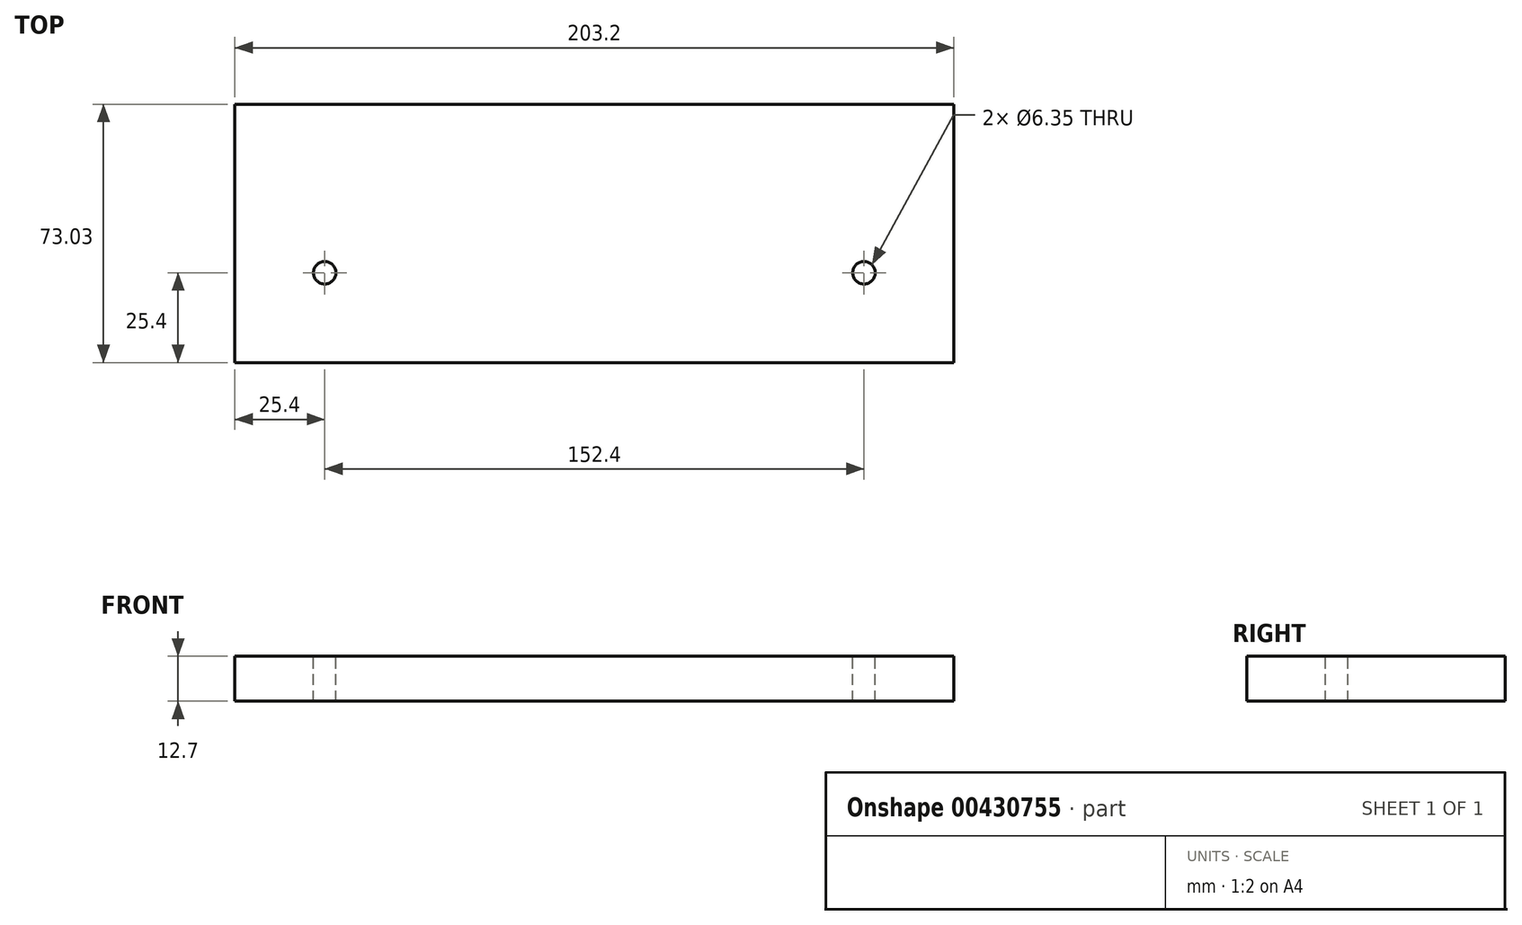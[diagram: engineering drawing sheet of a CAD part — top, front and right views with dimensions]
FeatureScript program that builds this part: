
annotation { "Feature Type Name" : "Feature", "Feature Type Description" : "" }
export const myFeature = defineFeature(function(context is Context, id is Id, definition is map)
    precondition{}
    {
        {
            var Q0;
            Q0=qCreatedBy(makeId("Top.planeOp"),FACE);
            var sketch = newSketch(context, id + "F0", { "sketchPlane" : qUnion([Q0])});
            skLineSegment(sketch, "E0.bottom", {"start": v(0, 0) * mm, "end": v(-203.2, 0) * mm});
            skLineSegment(sketch, "E0.top", {"start": v(0, 73.03) * mm, "end": v(-203.2, 73.02) * mm});
            skLineSegment(sketch, "E0.left", {"start": v(0, 0) * mm, "end": v(0, 73.03) * mm});
            skLineSegment(sketch, "E0.right", {"start": v(-203.2, 0) * mm, "end": v(-203.2, 73.03) * mm});
            skSolve(sketch);
        }
        {
            var Q0;
            Q0=makeQuery(id+"F0.imprint","IMPRINT",FACE,{"disambiguationData":[TD([[makeQuery(id+"F0.imprint","IMPRINT",EDGE,{"derivedFrom":sQuery(id+"F0.wireOp",EDGE,"E0.bottom")}),-1.0]])]});
            extrude(context, id + "F1", {"entities" : qUnion([Q0]), "depth" : 12.7 * mm, "offsetDistance" : 25.4 * mm});
        }
        {
            var Q0;
            Q0=makeQuery(id+"F1.opExtrude","CAP_FACE",FACE,{"disambiguationData":[OSD([sQuery(id+"F0.wireOp",EDGE,"E0.bottom"),sQuery(id+"F0.wireOp",EDGE,"E0.top"),sQuery(id+"F0.wireOp",EDGE,"E0.left"),sQuery(id+"F0.wireOp",EDGE,"E0.right")])],"isStart":false});
            var sketch = newSketch(context, id + "F2", { "sketchPlane" : qUnion([Q0])});
            skLineSegment(sketch, "E1", {"start": v(-203.2, 0) * mm, "end": v(-203.2, 25.4) * mm});
            skLineSegment(sketch, "E2", {"start": v(-203.2, 25.4) * mm, "end": v(-177.8, 25.4) * mm});
            skLineSegment(sketch, "E3", {"start": v(-177.8, 25.4) * mm, "end": v(-25.4, 25.4) * mm});
            skLineSegment(sketch, "E4", {"start": v(-25.4, 25.4) * mm, "end": v(0, 25.4) * mm});
            skCircle(sketch, "E5", {"center": v(-177.8, 25.4) * mm, "radius": 3.18 * mm});
            skCircle(sketch, "E6", {"center": v(-25.4, 25.4) * mm, "radius": 3.18 * mm});
            skSolve(sketch);
        }
        {
            var Q0;
            {var subQ0=sQuery(id+"F2.wireOp",EDGE,"E3");var subQ1=sQuery(id+"F2.wireOp",EDGE,"E2");var subQ2=makeQuery(id+"F2.imprint","INTERSECT",VERTEX,{"derivedFrom":[subQ1,subQ0]});Q0=makeQuery(id+"F2.imprint","IMPRINT",FACE,{"disambiguationData":[TD([[makeQuery(id+"F2.imprint","IMPRINT",EDGE,{"disambiguationData":[TD([[subQ2,1.0]])],"derivedFrom":subQ1}),-1.0]])]});}
            var Q1;
            {var subQ0=sQuery(id+"F2.wireOp",EDGE,"E3");var subQ1=sQuery(id+"F2.wireOp",EDGE,"E2");var subQ2=makeQuery(id+"F2.imprint","INTERSECT",VERTEX,{"derivedFrom":[subQ1,subQ0]});Q1=makeQuery(id+"F2.imprint","IMPRINT",FACE,{"disambiguationData":[TD([[makeQuery(id+"F2.imprint","IMPRINT",EDGE,{"disambiguationData":[TD([[subQ2,1.0]])],"derivedFrom":subQ1}),1.0]])]});}
            var Q2;
            {var subQ0=sQuery(id+"F2.wireOp",EDGE,"E4");var subQ1=sQuery(id+"F2.wireOp",EDGE,"E3");var subQ2=makeQuery(id+"F2.imprint","INTERSECT",VERTEX,{"derivedFrom":[subQ1,subQ0]});Q2=makeQuery(id+"F2.imprint","IMPRINT",FACE,{"disambiguationData":[TD([[makeQuery(id+"F2.imprint","IMPRINT",EDGE,{"disambiguationData":[TD([[subQ2,1.0]])],"derivedFrom":subQ1}),-1.0]])]});}
            var Q3;
            {var subQ0=sQuery(id+"F2.wireOp",EDGE,"E4");var subQ1=sQuery(id+"F2.wireOp",EDGE,"E3");var subQ2=makeQuery(id+"F2.imprint","INTERSECT",VERTEX,{"derivedFrom":[subQ1,subQ0]});Q3=makeQuery(id+"F2.imprint","IMPRINT",FACE,{"disambiguationData":[TD([[makeQuery(id+"F2.imprint","IMPRINT",EDGE,{"disambiguationData":[TD([[subQ2,1.0]])],"derivedFrom":subQ1}),1.0]])]});}
            extrude(context, id + "F3", {"entities" : qUnion([Q0, Q1, Q2, Q3]), "operationType" : NewBodyOperationType.REMOVE, "oppositeDirection" : true, "depth" : 25.4 * mm, "offsetDistance" : 25.4 * mm});
        }
    });
